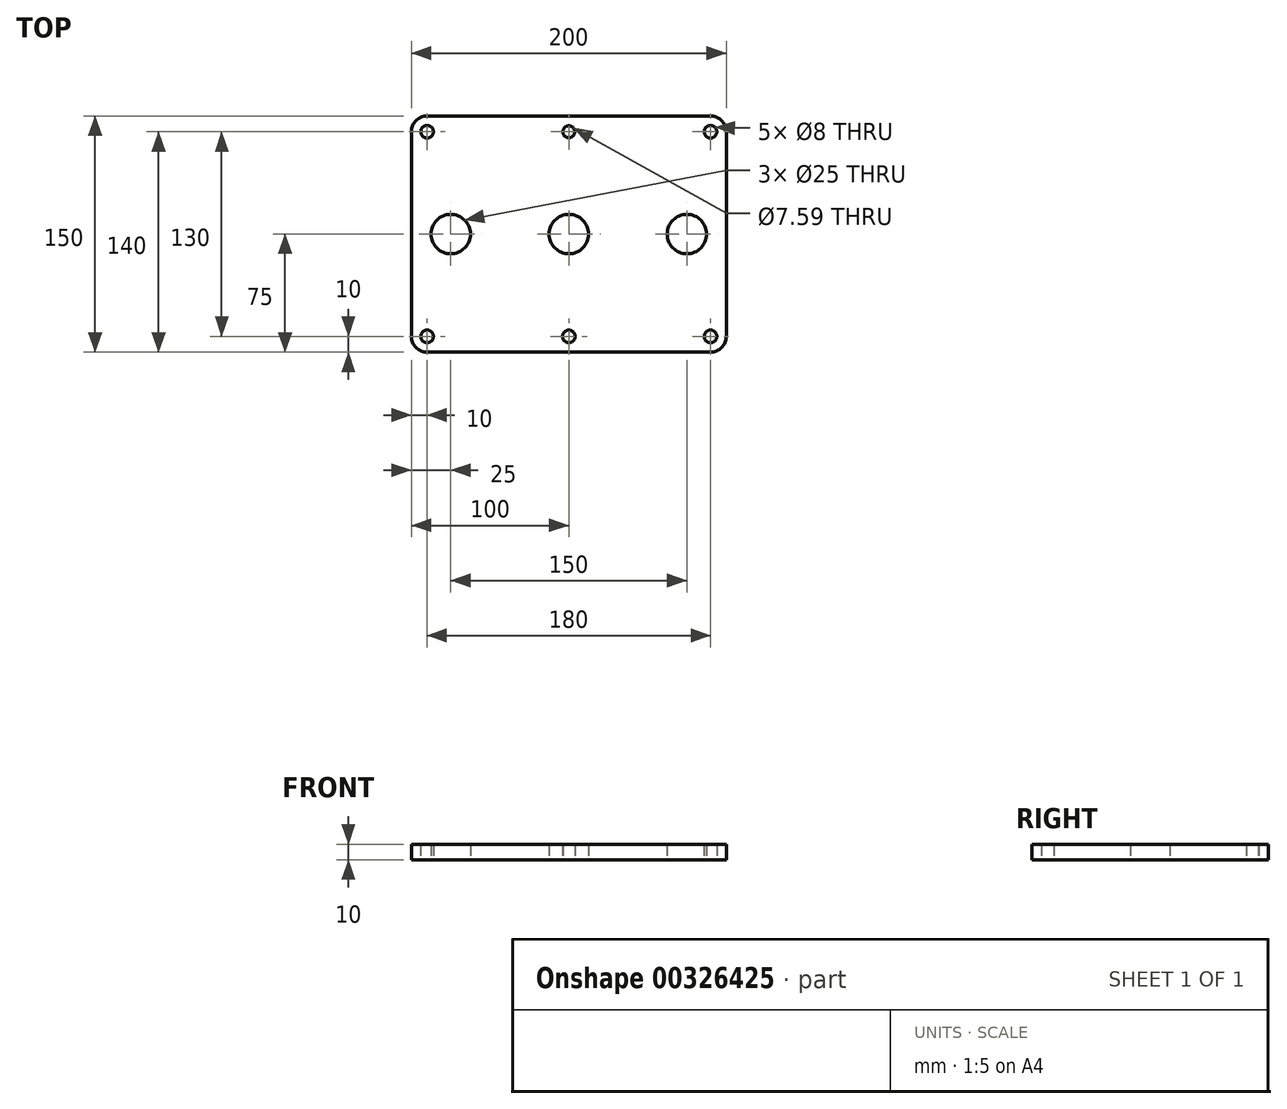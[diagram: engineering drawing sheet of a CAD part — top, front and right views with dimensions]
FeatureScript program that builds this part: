
annotation { "Feature Type Name" : "Feature", "Feature Type Description" : "" }
export const myFeature = defineFeature(function(context is Context, id is Id, definition is map)
    precondition{}
    {
        {
            var Q0;
            Q0=qCreatedBy(makeId("Top.planeOp"),FACE);
            var sketch = newSketch(context, id + "F0", { "sketchPlane" : qUnion([Q0])});
            skLineSegment(sketch, "E0.bottom", {"start": v(90, 75) * mm, "end": v(-90, 75) * mm});
            skLineSegment(sketch, "E0.top", {"start": v(90, -75) * mm, "end": v(-90, -75) * mm});
            skLineSegment(sketch, "E0.left", {"start": v(100, 65) * mm, "end": v(100, -65) * mm});
            skLineSegment(sketch, "E0.right", {"start": v(-100, 65) * mm, "end": v(-100, -65) * mm});
            skPoint(sketch, "E0.middle", {"position": v(0, 0) * mm});
            skPoint(sketch, "E1.visualSharp", {"position": v(-100, 75) * mm});
            skArc(sketch, "E1.filletArc", {"start": v(-90, 75) * mm, "mid": v(-97.07, 72.07) * mm, "end": v(-100, 65) * mm});
            skPoint(sketch, "E2.visualSharp", {"position": v(100, 75) * mm});
            skArc(sketch, "E2.filletArc", {"start": v(100, 65) * mm, "mid": v(97.07, 72.07) * mm, "end": v(90, 75) * mm});
            skPoint(sketch, "E3.visualSharp", {"position": v(100, -75) * mm});
            skArc(sketch, "E3.filletArc", {"start": v(90, -75) * mm, "mid": v(97.07, -72.07) * mm, "end": v(100, -65) * mm});
            skPoint(sketch, "E4.visualSharp", {"position": v(-100, -75) * mm});
            skArc(sketch, "E4.filletArc", {"start": v(-100, -65) * mm, "mid": v(-97.07, -72.07) * mm, "end": v(-90, -75) * mm});
            skPoint(sketch, "E5", {"position": v(0, 65) * mm});
            skPoint(sketch, "E6", {"position": v(0, -65) * mm});
            skCircle(sketch, "E7", {"center": v(-90, 65) * mm, "radius": 4 * mm});
            skCircle(sketch, "E8", {"center": v(0, 65) * mm, "radius": 3.8 * mm});
            skCircle(sketch, "E9", {"center": v(90, 65) * mm, "radius": 4 * mm});
            skCircle(sketch, "E10", {"center": v(90, -65) * mm, "radius": 4 * mm});
            skCircle(sketch, "E11", {"center": v(0, -65) * mm, "radius": 4 * mm});
            skCircle(sketch, "E12", {"center": v(-90, -65) * mm, "radius": 4 * mm});
            skPoint(sketch, "E13", {"position": v(-75, 0) * mm});
            skPoint(sketch, "E14", {"position": v(75, 0) * mm});
            skCircle(sketch, "E15", {"center": v(-75, 0) * mm, "radius": 12.5 * mm});
            skCircle(sketch, "E16", {"center": v(75, 0) * mm, "radius": 12.5 * mm});
            skCircle(sketch, "E17", {"center": v(0, 0) * mm, "radius": 12.5 * mm});
            skSolve(sketch);
        }
        {
            var Q0;
            Q0=makeQuery(id+"F0.imprint","IMPRINT",FACE,{"disambiguationData":[TD([[makeQuery(id+"F0.imprint","IMPRINT",EDGE,{"derivedFrom":sQuery(id+"F0.wireOp",EDGE,"E0.bottom")}),1.0]])]});
            extrude(context, id + "F1", {"entities" : qUnion([Q0]), "depth" : 10 * mm, "offsetDistance" : 25 * mm});
        }
    });
